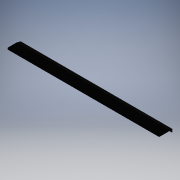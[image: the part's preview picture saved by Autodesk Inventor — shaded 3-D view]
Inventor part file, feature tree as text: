
AUTODESK INVENTOR PART (.ipt)
format: ipt  version: 2016 (Build 200138000, 138)  size: 103,424 bytes
history: native  units: mm
features: extrude x1, sketch x1
ambient origin geometry x8: Origin, YZ Plane, XZ Plane, XY Plane, X Axis, Y Axis, Z Axis, Center Point
bodies: Solid1 (feature_tree)
feature tree (2):
  extrude  "Extrusion1"  Depth=2.0mm
  sketch  "Sketch1"  dims[d6=15.0mm d9=2.0mm d10=779.45mm d11=0.0mm]
